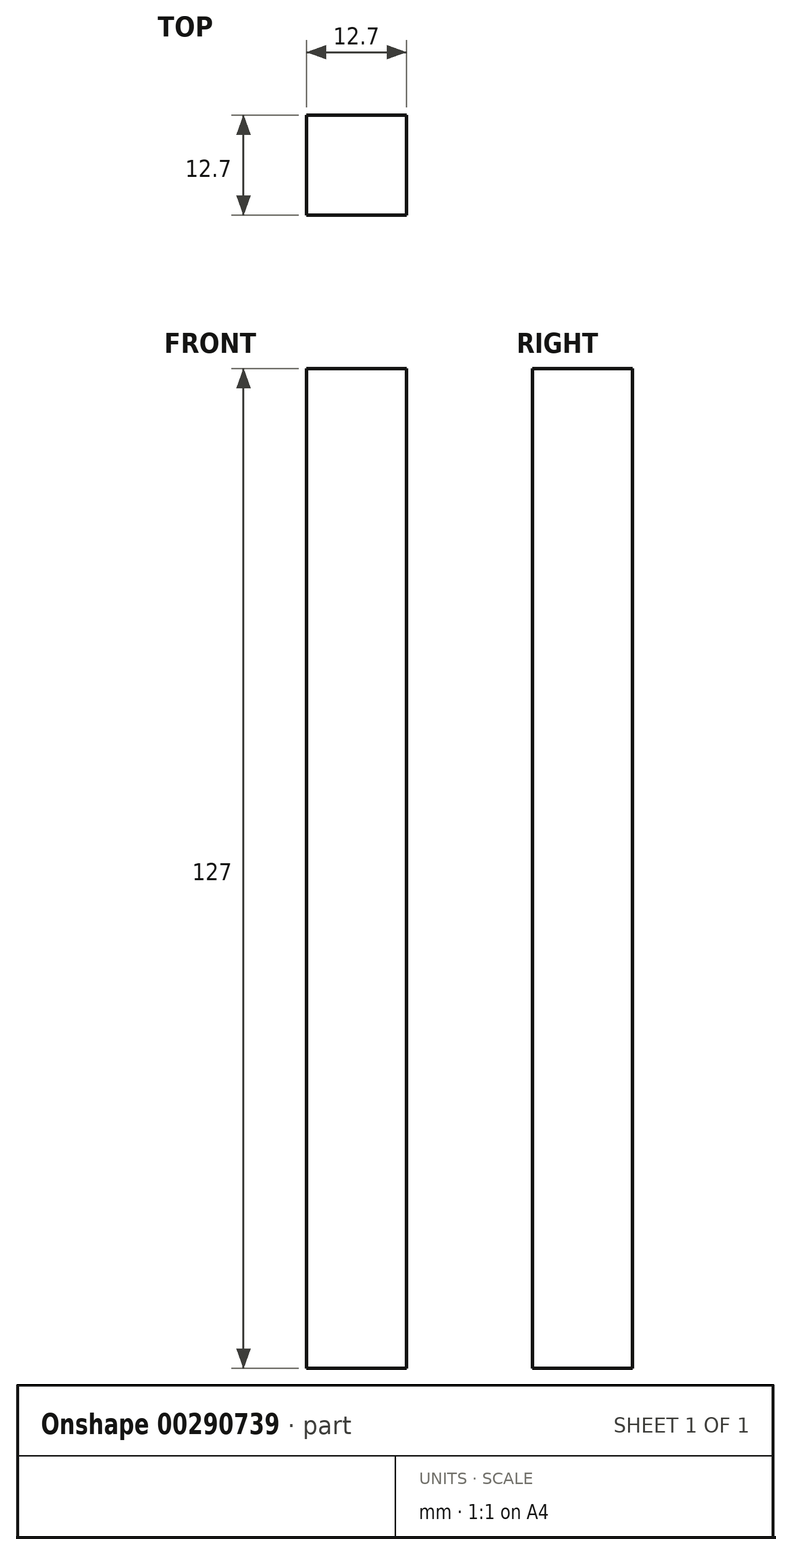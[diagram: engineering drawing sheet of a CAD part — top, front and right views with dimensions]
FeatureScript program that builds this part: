
annotation { "Feature Type Name" : "Feature", "Feature Type Description" : "" }
export const myFeature = defineFeature(function(context is Context, id is Id, definition is map)
    precondition{}
    {
        {
            var Q0;
            Q0=qCreatedBy(makeId("Front.planeOp"),FACE);
            var sketch = newSketch(context, id + "F0", { "sketchPlane" : qUnion([Q0])});
            skLineSegment(sketch, "E0.bottom", {"start": v(0, 0) * mm, "end": v(12.7, 0) * mm});
            skLineSegment(sketch, "E0.top", {"start": v(0, 127) * mm, "end": v(12.7, 127) * mm});
            skLineSegment(sketch, "E0.left", {"start": v(0, 0) * mm, "end": v(0, 127) * mm});
            skLineSegment(sketch, "E0.right", {"start": v(12.7, 0) * mm, "end": v(12.7, 127) * mm});
            skSolve(sketch);
        }
        {
            var Q0;
            Q0 = qSketchRegion(id + "F0", true);
            extrude(context, id + "F1", {"entities" : qUnion([Q0]), "depth" : 12.7 * mm});
        }
    });
